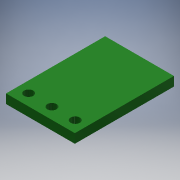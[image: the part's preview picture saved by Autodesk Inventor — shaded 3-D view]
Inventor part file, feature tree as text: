
AUTODESK INVENTOR PART (.ipt)
format: ipt  version: 2019 (Build 230136000, 136)  size: 122,880 bytes
history: mixed  units: in
note: dims shown in document units (in); Inventor stores cm internally (conversion verified against a paired STEP export)
features: reference x3, other x3, extrude x1, sketch x1, imported_body x1
ambient origin geometry x8: Origin, YZ Plane, XZ Plane, XY Plane, X Axis, Y Axis, Z Axis, Center Point
bodies: Solid1 (imported_parasolid)
feature tree (9):
  extrude  "Extrusion1"  Depth=0.0394in
  sketch  "Sketch1"  dims[d0=0.0394in d1=0.0394in d2=0.0394in d3=0.3937in d4=0.0in]
  reference  "Reference1"
  reference  "Reference2"
  reference  "Reference3"
  other  "Boss-Extrude1"
  other  "DD0503MA ULTRA MINI DC 3.7V 4.5V 5V TO 3.3V DC DC STEP DOWN CONVERTER BUCK MODULE.iam"
  other  "PIN HEADER, 1X3, 2.54 mm, DD0503MA ULTRA MINI DC 3.7V 4.5V 5V TO 3.3V DC DC STEP DOWN CONVERTE:1"
  imported_body  NMx_Import_Brep_tag  [imported B-rep: ~9 faces, bbox_mm=[7.5, 1.0, 10.8]]
